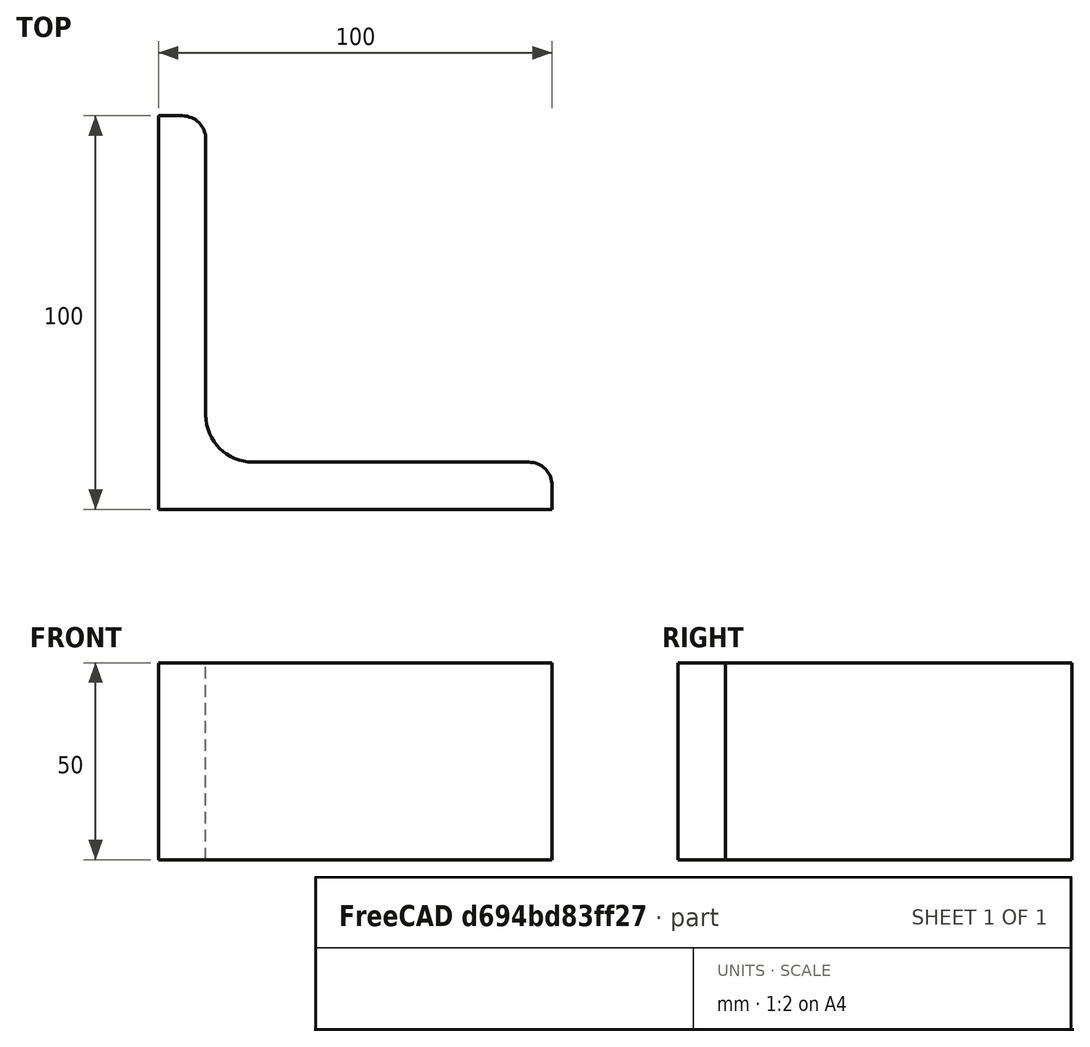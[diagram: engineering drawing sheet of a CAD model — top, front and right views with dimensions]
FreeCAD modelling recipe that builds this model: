
FCSTD DOCUMENT  (FreeCAD 0.15R4671 (Git))
Label: Angle Bar L100x100x12 EN10056 S235JR
License: All rights reserved
LicenseURL: http://en.wikipedia.org/wiki/All_rights_reserved
objects: Sketcher::SketchObject×1, Part::Extrusion×1
note: 2 computed .brp shape members not serialized (recipe doc carries the construction recipe); baked Part::Feature solids carry a one-line shape summary decoded from their .brp

FEATURE [Sketcher::SketchObject] Sketch
  sketch-geometry (9):
    g0: LineSegment StartX=0 StartY=0 StartZ=0 EndX=100 EndY=0 EndZ=0
    g1: LineSegment StartX=100 StartY=0 StartZ=0 EndX=100 EndY=6 EndZ=0
    g2: LineSegment StartX=94 StartY=12 StartZ=0 EndX=24 EndY=12 EndZ=0
    g3: LineSegment StartX=0 StartY=0 StartZ=0 EndX=0 EndY=100 EndZ=0
    g4: LineSegment StartX=0 StartY=100 StartZ=0 EndX=6 EndY=100 EndZ=0
    g5: LineSegment StartX=12 StartY=94 StartZ=0 EndX=12 EndY=24 EndZ=0
    g6: ArcOfCircle CenterX=24 CenterY=24 CenterZ=0 NormalX=0 NormalY=0 NormalZ=1 Radius=12 StartAngle=3.14159 EndAngle=4.71239
    g7: ArcOfCircle CenterX=6 CenterY=94 CenterZ=0 NormalX=0 NormalY=0 NormalZ=1 Radius=6 StartAngle=0 EndAngle=1.5708
    g8: ArcOfCircle CenterX=94 CenterY=6 CenterZ=0 NormalX=0 NormalY=0 NormalZ=1 Radius=6 StartAngle=0 EndAngle=1.5708
  constraints (23):
    c: Coincident(g0,g-1)
    c: Horizontal(g0)
    c: Coincident(g1,g0)
    c: Vertical(g1)
    c: Horizontal(g2)
    c: Coincident(g3,g-1)
    c: Vertical(g3)
    c: Coincident(g4,g3)
    c: Horizontal(g4)
    c: Vertical(g5)
    c: Tangent(g5,g6) = -1.5708
    c: Tangent(g2,g6) = 1.5708
    c: Tangent(g4,g7) = 1.5708
    c: Tangent(g5,g7) = 1.5708
    c: Tangent(g2,g8) = -1.5708
    c: Tangent(g1,g8) = -1.5708
    c: DistanceX(g0) = 100
    c: DistanceY(g3) = 100
    c: DistanceY(g0,g2) = 12
    c: DistanceX(g3,g5) = 12
    c: Radius(g6) = 12
    c: Radius(g8) = 6
    c: Radius(g7) = 6
FEATURE [Part::Extrusion] Extrude  label="Angle Bar L100x100x12 EN10056 S235JR"
  Base = -> Sketch
  Dir = (0,0,50)
  Solid = true
